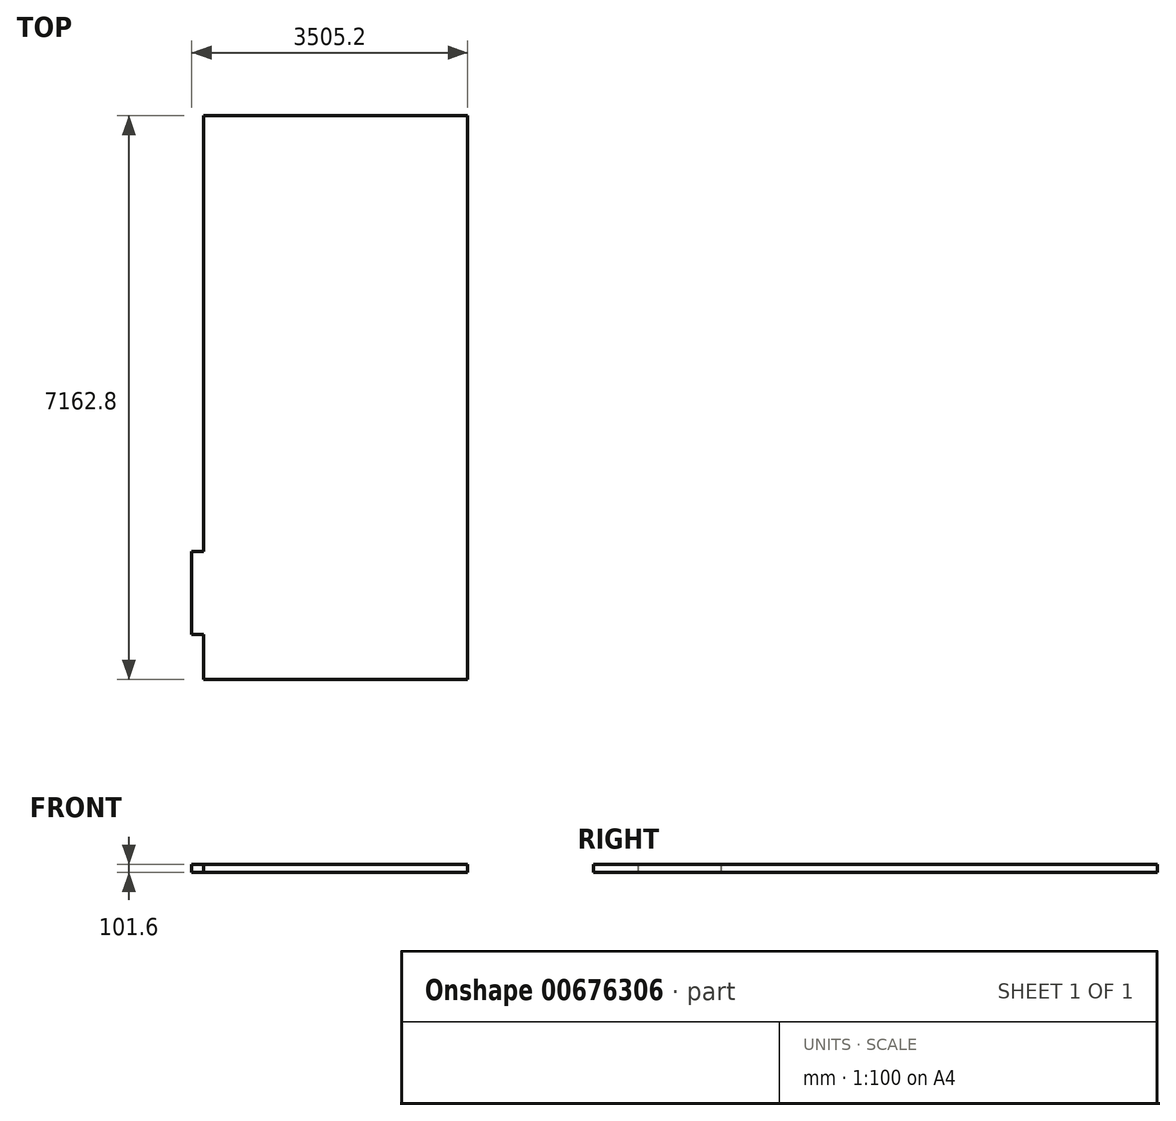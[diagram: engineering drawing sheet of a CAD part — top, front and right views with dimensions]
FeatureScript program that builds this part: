
annotation { "Feature Type Name" : "Feature", "Feature Type Description" : "" }
export const myFeature = defineFeature(function(context is Context, id is Id, definition is map)
    precondition{}
    {
        {
            var Q0;
            Q0=qCreatedBy(makeId("Top.planeOp"),FACE);
            var sketch = newSketch(context, id + "F0", { "sketchPlane" : qUnion([Q0])});
            skLineSegment(sketch, "E0.bottom", {"start": v(-1676.4, 3581.4) * mm, "end": v(1676.4, 3581.4) * mm});
            skLineSegment(sketch, "E0.top", {"start": v(-1676.4, -3581.4) * mm, "end": v(1676.4, -3581.4) * mm});
            skLineSegment(sketch, "E0.left", {"start": v(-1676.4, 3581.4) * mm, "end": v(-1676.4, -3581.4) * mm});
            skLineSegment(sketch, "E0.right", {"start": v(1676.4, 3581.4) * mm, "end": v(1676.4, -3581.4) * mm});
            skPoint(sketch, "E0.middle", {"position": v(0, 0) * mm});
            skSolve(sketch);
        }
        {
            var Q0;
            Q0 = qSketchRegion(id + "F0", true);
            extrude(context, id + "F1", {"entities" : qUnion([Q0]), "depth" : 101.6 * mm, "offsetDistance" : 25.4 * mm});
        }
        {
            var Q0;
            Q0=makeQuery(id+"F1.opExtrude","CAP_FACE",FACE,{"disambiguationData":[OSD([sQuery(id+"F0.wireOp",EDGE,"E0.bottom"),sQuery(id+"F0.wireOp",EDGE,"E0.top"),sQuery(id+"F0.wireOp",EDGE,"E0.left"),sQuery(id+"F0.wireOp",EDGE,"E0.right")])],"isStart":false});
            var sketch = newSketch(context, id + "F2", { "sketchPlane" : qUnion([Q0])});
            skLineSegment(sketch, "E1.bottom", {"start": v(-1676.4, -3009.9) * mm, "end": v(-1828.8, -3009.9) * mm});
            skLineSegment(sketch, "E1.top", {"start": v(-1676.4, -1955.8) * mm, "end": v(-1828.8, -1955.8) * mm});
            skLineSegment(sketch, "E1.left", {"start": v(-1676.4, -3009.9) * mm, "end": v(-1676.4, -1955.8) * mm});
            skLineSegment(sketch, "E1.right", {"start": v(-1828.8, -3009.9) * mm, "end": v(-1828.8, -1955.8) * mm});
            skSolve(sketch);
        }
        {
            var Q0;
            Q0 = qSketchRegion(id + "F2", true);
            var Q1;
            Q1=makeQuery(id+"F1.opExtrude","CAP_FACE",FACE,{"disambiguationData":[OSD([sQuery(id+"F0.wireOp",EDGE,"E0.bottom"),sQuery(id+"F0.wireOp",EDGE,"E0.top"),sQuery(id+"F0.wireOp",EDGE,"E0.left"),sQuery(id+"F0.wireOp",EDGE,"E0.right")])],"isStart":true});
            extrude(context, id + "F3", {"entities" : qUnion([Q0]), "operationType" : NewBodyOperationType.ADD, "endBound" : BoundingType.UP_TO_SURFACE, "oppositeDirection" : true, "depth" : 25.4 * mm, "endBoundEntityFace" : qUnion([Q1]), "offsetDistance" : 25.4 * mm});
        }
    });
